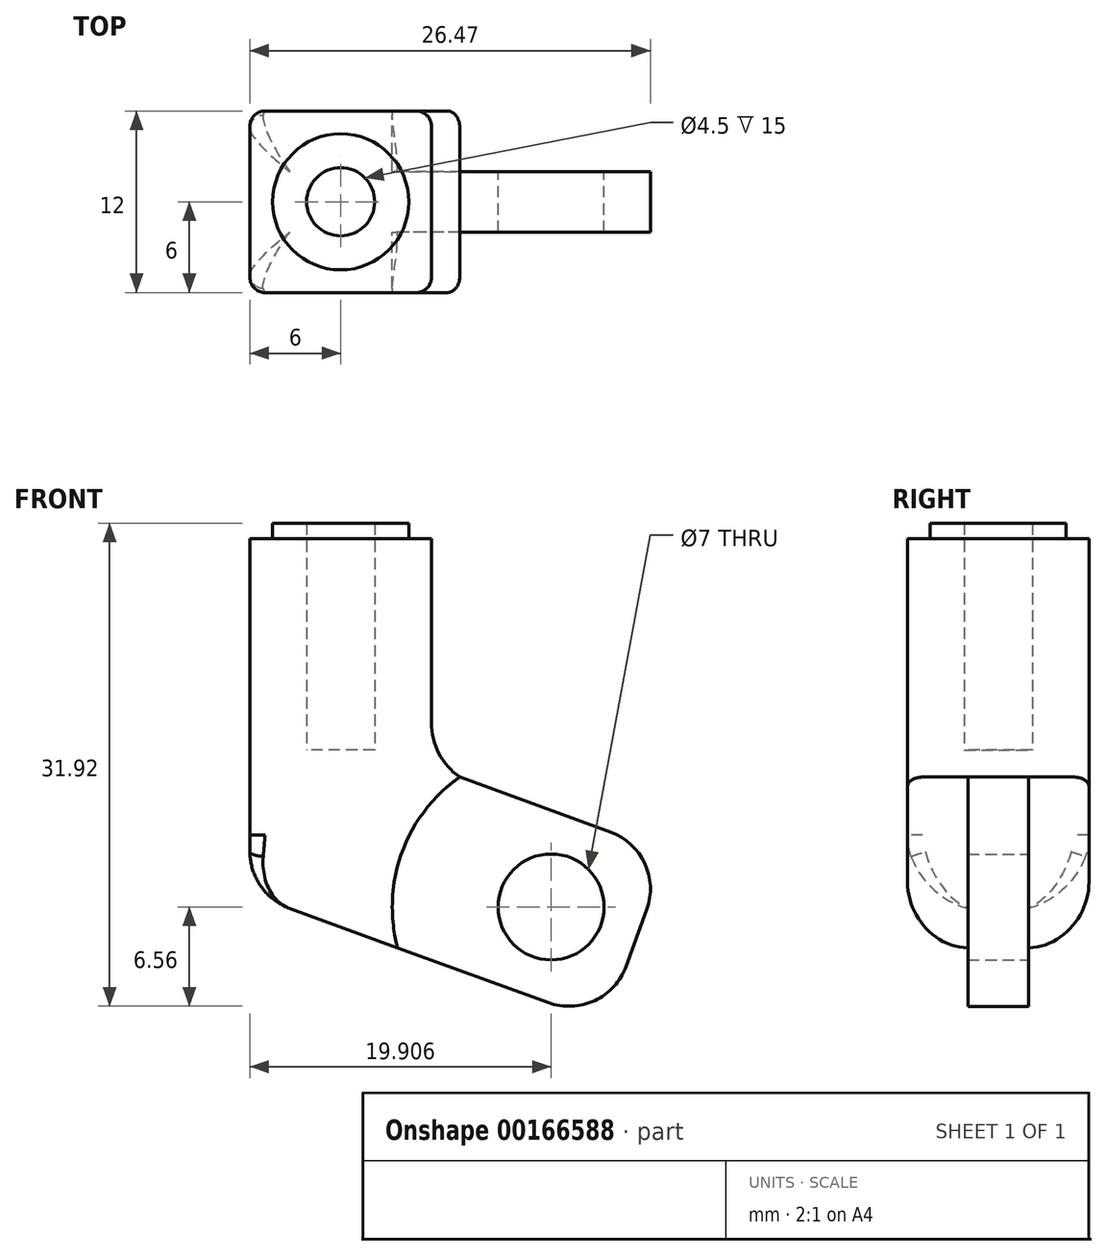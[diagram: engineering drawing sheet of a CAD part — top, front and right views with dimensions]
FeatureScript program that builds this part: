
annotation { "Feature Type Name" : "Feature", "Feature Type Description" : "" }
export const myFeature = defineFeature(function(context is Context, id is Id, definition is map)
    precondition{}
    {
        {
            var Q0;
            Q0=qCreatedBy(makeId("Front.planeOp"),FACE);
            var sketch = newSketch(context, id + "F0", { "sketchPlane" : qUnion([Q0])});
            skLineSegment(sketch, "E0.bottom", {"start": v(-6, 0) * mm, "end": v(6, 0) * mm});
            skLineSegment(sketch, "E0.left", {"start": v(-6, 0) * mm, "end": v(-6, -20) * mm});
            skLineSegment(sketch, "E0.right", {"start": v(6, 0) * mm, "end": v(6, -11.6) * mm});
            skLineSegment(sketch, "E1", {"start": v(-6, -20) * mm, "end": v(17.5, -28.55) * mm});
            skLineSegment(sketch, "E2", {"start": v(17.5, -28.55) * mm, "end": v(21.6, -17.27) * mm});
            skLineSegment(sketch, "E3", {"start": v(21.6, -17.27) * mm, "end": v(6, -11.6) * mm});
            skSolve(sketch);
        }
        {
            var Q0;
            Q0=makeQuery(id+"F0.imprint","IMPRINT",FACE,{"disambiguationData":[TD([[makeQuery(id+"F0.imprint","IMPRINT",EDGE,{"derivedFrom":sQuery(id+"F0.wireOp",EDGE,"E0.bottom")}),-1.0]])]});
            extrude(context, id + "F1", {"entities" : qUnion([Q0]), "depth" : 12 * mm, "symmetric" : true});
        }
        {
            var Q0;
            Q0=qCreatedBy(makeId("Top.planeOp"),FACE);
            var sketch = newSketch(context, id + "F2", { "sketchPlane" : qUnion([Q0])});
            skCircle(sketch, "E4", {"center": v(0, 0) * mm, "radius": 4.5 * mm});
            skCircle(sketch, "E5", {"center": v(0, 0) * mm, "radius": 2.25 * mm});
            skSolve(sketch);
        }
        {
            var Q0;
            Q0=makeQuery(id+"F2.imprint","IMPRINT",FACE,{"disambiguationData":[TD([[makeQuery(id+"F2.imprint","IMPRINT",EDGE,{"derivedFrom":sQuery(id+"F2.wireOp",EDGE,"E4")}),1.0]])]});
            extrude(context, id + "F3", {"entities" : qUnion([Q0]), "operationType" : NewBodyOperationType.ADD, "depth" : 4.5 * mm});
        }
        {
            var Q0;
            Q0=makeQuery(id+"F3.boolean.opBoolean","SPLIT",FACE,{"disambiguationData":[TD([makeQuery(id+"F3.opExtrude","SWEPT_FACE",FACE,{"disambiguationData":[OSD([sQuery(id+"F2.wireOp",EDGE,"E5")])]})])],"derivedFrom":makeQuery(id+"F1.opExtrude","SWEPT_FACE",FACE,{"disambiguationData":[OSD([sQuery(id+"F0.wireOp",EDGE,"E0.bottom")])]})});
            extrude(context, id + "F4", {"entities" : qUnion([Q0]), "operationType" : NewBodyOperationType.REMOVE, "oppositeDirection" : true, "depth" : 10.5 * mm});
        }
        {
            var Q0;
            Q0=qCreatedBy(makeId("Front.planeOp"),FACE);
            var sketch = newSketch(context, id + "F5", { "sketchPlane" : qUnion([Q0])});
            skLineSegment(sketch, "E6", {"start": v(28.45, -26.15) * mm, "end": v(-10.23, -12.07) * mm, "construction": true});
            skLineSegment(sketch, "E7", {"start": v(18.48, -8.3) * mm, "end": v(9.58, -32.74) * mm, "construction": true});
            skArc(sketch, "E8", {"start": v(7.86, -12.27) * mm, "mid": v(4.04, -17.27) * mm, "end": v(3.76, -23.55) * mm});
            skPoint(sketch, "E9", {"position": v(7.86, -12.27) * mm});
            skPoint(sketch, "E10", {"position": v(3.76, -23.55) * mm});
            skLineSegment(sketch, "E11", {"start": v(7.86, -12.27) * mm, "end": v(21.6, -17.27) * mm});
            skLineSegment(sketch, "E12", {"start": v(21.6, -17.27) * mm, "end": v(17.5, -28.55) * mm});
            skLineSegment(sketch, "E13", {"start": v(17.5, -28.55) * mm, "end": v(3.76, -23.55) * mm});
            skCircle(sketch, "E14", {"center": v(13.9, -20.86) * mm, "radius": 3.5 * mm});
            skSolve(sketch);
        }
        {
            var Q0;
            Q0=qCreatedBy(makeId("Front.planeOp"),FACE);
            var sketch = newSketch(context, id + "F6", { "sketchPlane" : qUnion([Q0])});
            skLineSegment(sketch, "E15", {"start": v(28.45, -26.15) * mm, "end": v(-10.23, -12.07) * mm, "construction": true});
            skLineSegment(sketch, "E16", {"start": v(18.48, -8.3) * mm, "end": v(9.58, -32.74) * mm, "construction": true});
            skArc(sketch, "E17", {"start": v(7.86, -12.27) * mm, "mid": v(4.04, -17.27) * mm, "end": v(3.76, -23.55) * mm});
            skPoint(sketch, "E18", {"position": v(7.86, -12.27) * mm});
            skPoint(sketch, "E19", {"position": v(3.76, -23.55) * mm});
            skLineSegment(sketch, "E20", {"start": v(7.86, -12.27) * mm, "end": v(21.6, -17.27) * mm});
            skLineSegment(sketch, "E21", {"start": v(21.6, -17.27) * mm, "end": v(17.5, -28.55) * mm});
            skLineSegment(sketch, "E22", {"start": v(17.5, -28.55) * mm, "end": v(3.76, -23.55) * mm});
            skLineSegment(sketch, "E23", {"start": v(-9.94, -29.86) * mm, "end": v(26.33, -29.86) * mm, "construction": true});
            skSolve(sketch);
        }
        {
            var Q0;
            Q0 = qSketchRegion(id + "F6", true);
            extrude(context, id + "F7", {"entities" : qUnion([Q0]), "operationType" : NewBodyOperationType.REMOVE, "depth" : 12 * mm, "symmetric" : true});
        }
        {
            var Q0;
            Q0=makeQuery(id+"F5.imprint","IMPRINT",FACE,{"disambiguationData":[TD([[makeQuery(id+"F5.imprint","IMPRINT",EDGE,{"derivedFrom":sQuery(id+"F5.wireOp",EDGE,"E8")}),1.0]])]});
            extrude(context, id + "F8", {"entities" : qUnion([Q0]), "depth" : 4 * mm, "hasSecondDirection" : true, "secondDirectionOppositeDirection" : true, "secondDirectionDepth" : 3 * mm, "symmetric" : true});
        }
        {
            var Q0;
            Q0=makeQuery(id+"F1.opExtrude","SWEPT_EDGE",EDGE,{"disambiguationData":[OSD([sQuery(id+"F0.wireOp",EDGE,"E0.right"),sQuery(id+"F0.wireOp",EDGE,"E3")])]});
            fillet(context, id + "F9", {"entities" : qUnion([Q0]), "radius" : 4.4 * mm, "tangentPropagation" : true, "allowEdgeOverflow" : false});
        }
        {
            var Q0;
            Q0=makeQuery(id+"F8.opExtrude","SWEPT_EDGE",EDGE,{"disambiguationData":[OSD([sQuery(id+"F5.wireOp",EDGE,"E11"),sQuery(id+"F5.wireOp",EDGE,"E12")])]});
            var Q1;
            Q1=makeQuery(id+"F8.opExtrude","SWEPT_EDGE",EDGE,{"disambiguationData":[OSD([sQuery(id+"F5.wireOp",EDGE,"E12"),sQuery(id+"F5.wireOp",EDGE,"E13")])]});
            fillet(context, id + "F10", {"entities" : qUnion([Q0, Q1]), "radius" : 4 * mm, "tangentPropagation" : true, "allowEdgeOverflow" : false});
        }
        {
            var Q0;
            Q0=makeQuery(id+"F1.opExtrude","CAP_EDGE",EDGE,{"disambiguationData":[OSD([sQuery(id+"F0.wireOp",EDGE,"E0.left")])],"isStart":false});
            var Q1;
            Q1=makeQuery(id+"F1.opExtrude","CAP_EDGE",EDGE,{"disambiguationData":[OSD([sQuery(id+"F0.wireOp",EDGE,"E0.left")])],"isStart":true});
            var Q2;
            Q2=makeQuery(id+"F1.opExtrude","CAP_EDGE",EDGE,{"disambiguationData":[OSD([sQuery(id+"F0.wireOp",EDGE,"E0.right")])],"isStart":false});
            var Q3;
            Q3=makeQuery(id+"F1.opExtrude","CAP_EDGE",EDGE,{"disambiguationData":[OSD([sQuery(id+"F0.wireOp",EDGE,"E0.right")])],"isStart":true});
            fillet(context, id + "F11", {"entities" : qUnion([Q0, Q1, Q2, Q3]), "radius" : 1 * mm, "tangentPropagation" : true, "allowEdgeOverflow" : false});
        }
        {
            var Q0;
            Q0=makeQuery(id+"F1.opExtrude","CAP_EDGE",EDGE,{"disambiguationData":[OSD([sQuery(id+"F0.wireOp",EDGE,"E1")])],"isStart":false});
            fillet(context, id + "F12", {"entities" : qUnion([Q0]), "radius" : 4 * mm, "tangentPropagation" : true, "allowEdgeOverflow" : false});
        }
        {
            var Q0;
            Q0=makeQuery(id+"F1.opExtrude","SWEPT_BODY",BODY,{"disambiguationData":[OSD([sQuery(id+"F0.wireOp",EDGE,"E0.bottom"),sQuery(id+"F0.wireOp",EDGE,"E0.left"),sQuery(id+"F0.wireOp",EDGE,"E0.right"),sQuery(id+"F0.wireOp",EDGE,"E1"),sQuery(id+"F0.wireOp",EDGE,"E2"),sQuery(id+"F0.wireOp",EDGE,"E3")])]});
            var Q1;
            Q1=makeQuery(id+"F8.opExtrude","SWEPT_BODY",BODY,{"disambiguationData":[OSD([sQuery(id+"F5.wireOp",EDGE,"E8"),sQuery(id+"F5.wireOp",EDGE,"E11"),sQuery(id+"F5.wireOp",EDGE,"E12"),sQuery(id+"F5.wireOp",EDGE,"E13"),sQuery(id+"F5.wireOp",EDGE,"E14")])]});
            booleanBodies(context, id + "F13", {"operationType" : BooleanOperationType.UNION, "tools" : qUnion([Q0, Q1])});
        }
        {
            var Q0;
            {var subQ1=sQuery(id+"F0.wireOp",EDGE,"E0.left");var subQ5=sQuery(id+"F0.wireOp",EDGE,"E0.bottom");Q0=makeQuery(id+"F3.boolean.opBoolean","SPLIT",FACE,{"disambiguationData":[TD([makeQuery(id+"F1.opExtrude","SWEPT_FACE",FACE,{"disambiguationData":[OSD([subQ1])]})])],"derivedFrom":makeQuery(id+"F1.opExtrude","SWEPT_FACE",FACE,{"disambiguationData":[OSD([subQ5])]})});}
            extrude(context, id + "F14", {"entities" : qUnion([Q0]), "operationType" : NewBodyOperationType.ADD, "depth" : 3.5 * mm});
        }
    });
